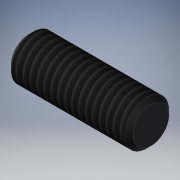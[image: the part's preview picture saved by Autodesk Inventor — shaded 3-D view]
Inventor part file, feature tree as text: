
AUTODESK INVENTOR PART (.ipt)
format: ipt  version: 2019 (Build 230136000, 136)  size: 131,584 bytes
history: native  units: mm
features: other x14, revolve x1, thread x1, sketch x1
ambient origin geometry x8: Origin, YZ Plane, XZ Plane, XY Plane, X Axis, Y Axis, Z Axis, Center Point
bodies: Solid1 (feature_tree)
feature tree (17):
  revolve  "Revolution1"  [1 undecoded]
  thread  "Thread1"  [1 undecoded]
  other  "mdk_1_XY"
  other  "mdk_1_YZ"
  other  "mdk_1_ZX"
  other  "mdk_1_X"
  other  "mdk_1_Y"
  other  "mdk_1_Z"
  other  "mdk_1_Center"
  other  "mdk_d_XY"
  other  "mdk_d_YZ"
  other  "mdk_d_ZX"
  other  "mdk_d_X"
  other  "mdk_d_Y"
  other  "mdk_d_Z"
  other  "mdk_d_Center"
  sketch  "Sketch_2"  dims[d0=360.0deg d1=20.466mm d2=0.0mm d3=0.0mm]
note: 2 required parameter values undecoded (feature->parameter linkage not recoverable at this tier; creation-order binding heuristic only, values carry confidence <= 0.55)